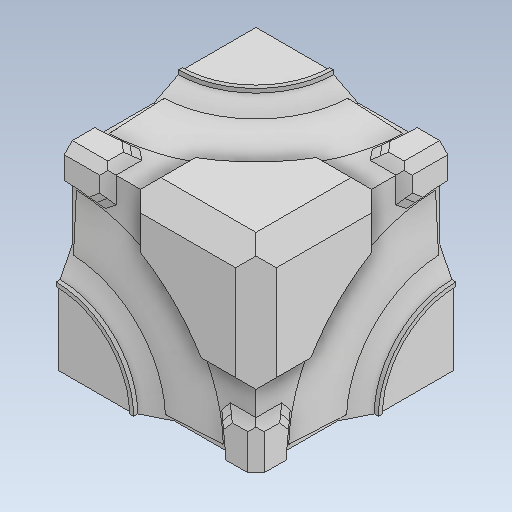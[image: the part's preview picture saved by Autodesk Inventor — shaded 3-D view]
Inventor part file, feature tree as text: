
AUTODESK INVENTOR PART (.ipt)
format: ipt  version: 2020 (Build 240168000, 168)  size: 492,544 bytes
history: native  units: in
note: dims shown in document units (in); Inventor stores cm internally (conversion verified against a paired STEP export)
features: chamfer x37, extrude x12, sketch x12, plane x2, mirror x2
ambient origin geometry x8: Origin, YZ Plane, XZ Plane, XY Plane, X Axis, Y Axis, Z Axis, Center Point
bodies: Solid1 (feature_tree)
feature tree (65):
  extrude  "Extrusion1"  Depth=0.5in
  extrude  "Extrusion2"  Depth=0.333in
  extrude  "Extrusion3"  Depth=0.05in TaperAngle=0.0deg
  extrude  "Extrusion4"  Depth=0.06in
  extrude  "Extrusion5"  Depth=0.75in
  chamfer  "Chamfer2"  Distance=0.05in
  extrude  "Extrusion6"  Depth=0.02in TaperAngle=0.0deg
  extrude  "Extrusion7"  Depth=0.01in
  extrude  "Extrusion8"  Depth=0.5in
  extrude  "Extrusion9"  Depth=0.74in
  plane  "Work Plane3"
  mirror  "Mirror2"
  plane  "Work Plane4"
  mirror  "Mirror3"
  extrude  "Extrusion10"  Depth=0.5in
  extrude  "Extrusion11"  Depth=0.38in
  extrude  "Extrusion12"  Depth=0.36in
  chamfer  "Chamfer13"  Distance=0.005in
  chamfer  "Chamfer14"  Distance=0.03in
  chamfer  "Chamfer15"  Distance=0.03in
  chamfer  "Chamfer16"  Distance=0.03in
  chamfer  "Chamfer17"  Distance=0.06in Angle=45.0deg
  chamfer  "Chamfer18"  Distance=0.06in Angle=45.0deg
  chamfer  "Chamfer19"  Distance=0.03in Angle=45.0deg
  chamfer  "Chamfer20"  Distance=0.05in Angle=45.0deg
  chamfer  "Chamfer21"  Distance=0.05in Angle=45.0deg
  chamfer  "Chamfer22"  Distance=0.05in Angle=45.0deg
  chamfer  "Chamfer23"  Distance=0.05in Angle=45.0deg
  chamfer  "Chamfer24"  Distance=0.05in Angle=45.0deg
  chamfer  "Chamfer25"  Distance=0.05in Angle=45.0deg
  chamfer  "Chamfer26"  Distance=0.05in Angle=45.0deg
  chamfer  "Chamfer27"  Distance=0.05in Angle=45.0deg
  chamfer  "Chamfer28"  Distance=0.05in Angle=45.0deg
  chamfer  "Chamfer29"  Distance=0.05in Angle=45.0deg
  chamfer  "Chamfer30"  Distance=0.05in Angle=45.0deg
  chamfer  "Chamfer31"  Distance=0.05in Angle=45.0deg
  chamfer  "Chamfer32"  Distance=0.02in Angle=45.0deg
  chamfer  "Chamfer33"  Distance=0.02in Angle=45.0deg
  chamfer  "Chamfer34"  Distance=0.02in Angle=45.0deg
  chamfer  "Chamfer35"  Distance=0.02in Angle=45.0deg
  chamfer  "Chamfer36"  Distance=0.02in Angle=45.0deg
  chamfer  "Chamfer37"  Distance=0.02in Angle=45.0deg
  chamfer  "Chamfer39"  Distance=0.02in Angle=45.0deg
  chamfer  "Chamfer40"  Distance=0.02in Angle=45.0deg
  chamfer  "Chamfer41"  Distance=0.02in Angle=45.0deg
  chamfer  "Chamfer42"  Distance=0.02in Angle=45.0deg
  chamfer  "Chamfer43"  Distance=0.02in Angle=45.0deg
  chamfer  "Chamfer44"  Distance=0.02in Angle=45.0deg
  chamfer  "Chamfer45"  Distance=0.02in Angle=45.0deg
  chamfer  "Chamfer46"  Distance=0.02in Angle=45.0deg
  chamfer  "Chamfer47"  Distance=0.02in Angle=45.0deg
  chamfer  "Chamfer48"  Distance=0.02in Angle=45.0deg
  chamfer  "Chamfer49"  Distance=0.02in Angle=45.0deg
  sketch  "Sketch1"  dims[d0=0.5in d1=0.5in]
  sketch  "Sketch2"  dims[d2=0.5in d3=0.0in d4=0.333in]
  sketch  "Sketch3"  dims[d5=0.333in d6=0.05in d7=0.0in]
  sketch  "Sketch4"  dims[d8=0.06in d9=0.06in]
  sketch  "Sketch5"  dims[d10=0.02in d11=0.0in d12=0.75in d13=0.05in d14=0.0in]
  sketch  "Sketch7"  dims[d15=0.74in d16=0.02in d17=0.0in]
  sketch  "Sketch8"  dims[d23=0.37in d24=0.02in d25=45.0deg d26=0.01in]
  sketch  "Sketch9"  dims[d27=0.5in d28=0.5in]
  sketch  "Sketch10"  dims[d29=0.01in d30=0.74in]
  sketch  "Sketch13"  dims[d31=0.02in d32=0.0in d33=0.5in]
  sketch  "Sketch14"  dims[d34=0.03in d35=0.0in d36=0.38in]
  sketch  "Sketch15"  dims[d37=0.01in d38=0.0in d39=0.36in d40=0.005in d41=0.0in d73=0.03in d74=0.0in d75=0.03in d76=0.0in d77=0.03in d78=0.0in d79=0.06in d80=0.03in d81=45.0deg d82=0.06in d83=0.03in d84=45.0deg d85=0.03in d86=0.06in d87=45.0deg d88=0.05in d89=0.05in d90=45.0deg d91=0.05in d92=0.05in d93=45.0deg d94=0.05in d95=0.05in d96=45.0deg d97=0.05in d98=0.05in d99=45.0deg d100=0.05in d101=0.05in d102=45.0deg d103=0.05in d104=0.05in d105=45.0deg d106=0.05in d107=0.05in d108=45.0deg d109=0.05in d110=0.05in d111=45.0deg d112=0.05in d113=0.05in d114=45.0deg d115=0.05in d116=0.05in d117=45.0deg d118=0.05in d119=0.05in d120=45.0deg d121=0.05in d122=0.05in d123=45.0deg d124=0.02in d125=0.02in d126=45.0deg d127=0.02in d128=0.02in d129=45.0deg d130=0.02in d131=0.02in d132=45.0deg d133=0.02in d134=0.02in d135=45.0deg d136=0.02in d137=0.02in d138=45.0deg d139=0.02in d140=0.02in d141=45.0deg d142=0.02in d143=0.02in d144=45.0deg d145=0.02in d146=0.02in d147=45.0deg d148=0.02in d149=0.02in d150=45.0deg d151=0.02in d152=0.02in d153=45.0deg d157=0.02in d158=0.02in d159=45.0deg d160=0.02in d161=0.02in d162=45.0deg d163=0.02in d164=0.02in d165=45.0deg d166=0.02in d167=0.02in d168=45.0deg d169=0.02in d170=0.02in d171=45.0deg d172=0.02in d173=0.02in d174=45.0deg d175=0.02in d176=0.02in d177=45.0deg d178=0.02in d179=0.02in d180=45.0deg d181=0.02in d182=0.02in d183=45.0deg d184=0.02in d185=0.02in d186=45.0deg d187=0.02in d188=0.02in d189=45.0deg]
